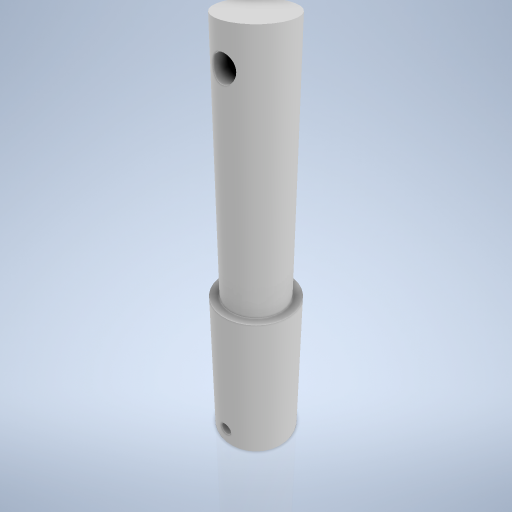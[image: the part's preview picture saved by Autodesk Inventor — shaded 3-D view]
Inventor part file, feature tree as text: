
AUTODESK INVENTOR PART (.ipt)
format: ipt  version: 2024.2 (Build 282272000, 272)  size: 285,696 bytes
history: native  units: mm
features: sketch x2, hole x2, revolve x1, plane x1, projected_geometry x1
ambient origin geometry x8: Origin, YZ Plane, XZ Plane, XY Plane, X Axis, Y Axis, Z Axis, Center Point
bodies: Volumenkörper1 (feature_tree)
feature tree (7):
  revolve  "Umdrehung1"
  plane  "Arbeitsebene1"
  sketch  "Skizze2"  dims[d8=28.0mm d11=90.0deg d12=176.0mm d13=36.0mm d14=70.0mm d15=18.0mm d16=8.0mm d17=14.0mm d18=6.0mm d19=6.0mm d20=4.0mm d21=2.0mm d22=90.0deg d23=8.0mm d24=20.594885mm d25=10.0mm d26=6.0mm d27=4.0mm d28=2.0mm d29=90.0deg d30=8.0mm d31=20.594885mm]
  hole  "Bohrung1"  [1 undecoded]
  hole  "Bohrung2"  [1 undecoded]
  sketch  "Skizze1"  dims[d3=36.0mm d6=78.0mm]
  projected_geometry  "Projizierte Kontur1"
note: 2 required parameter values undecoded (feature->parameter linkage not recoverable at this tier; creation-order binding heuristic only, values carry confidence <= 0.55)
